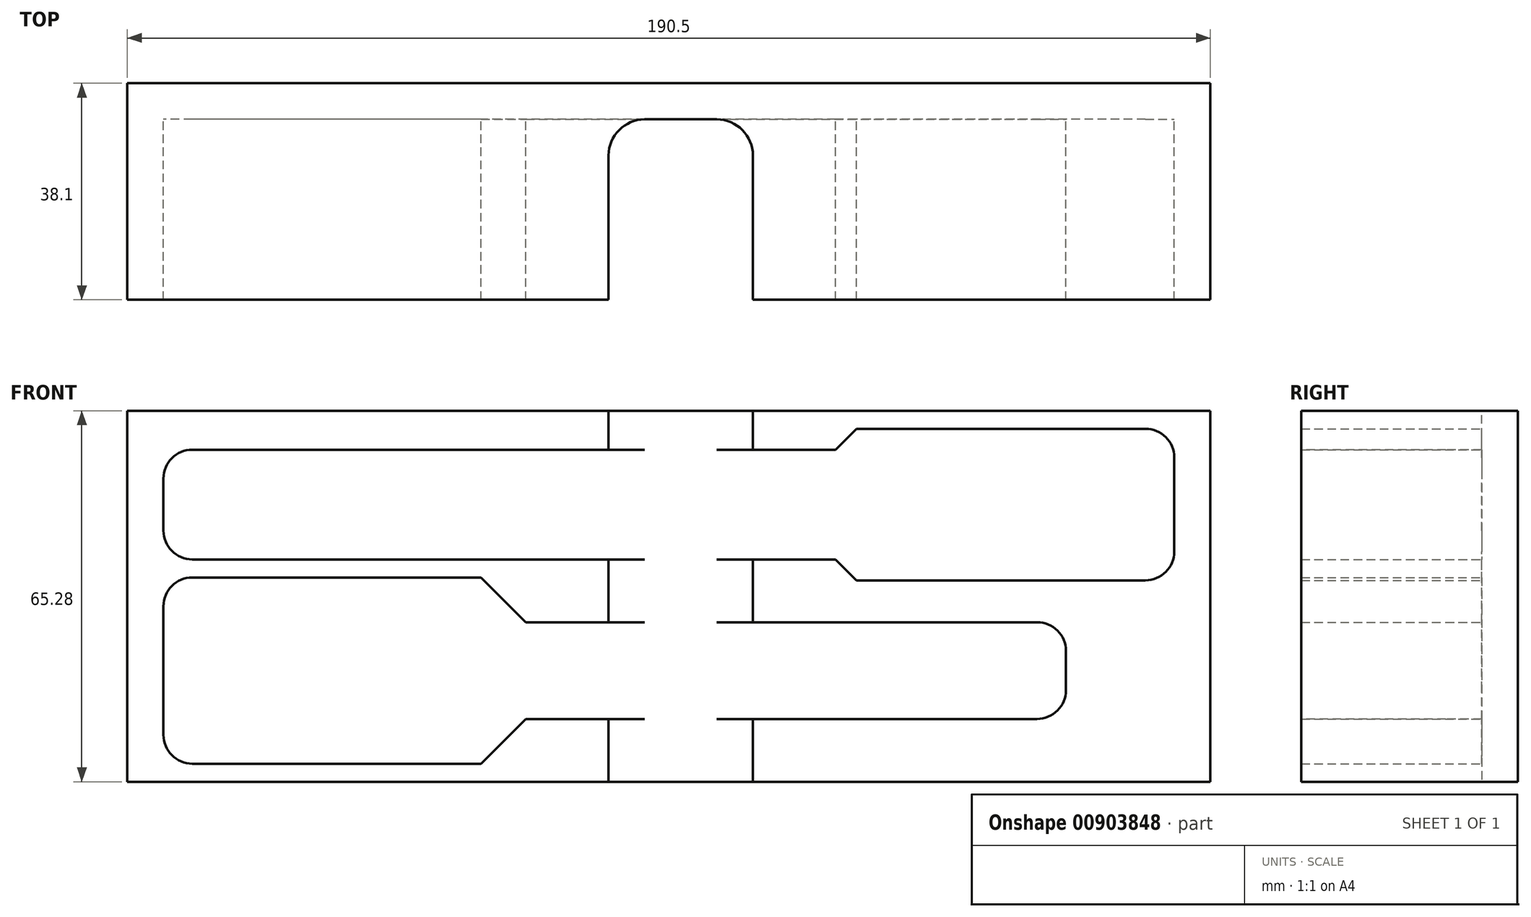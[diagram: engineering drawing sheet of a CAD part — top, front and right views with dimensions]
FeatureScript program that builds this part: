
annotation { "Feature Type Name" : "Feature", "Feature Type Description" : "" }
export const myFeature = defineFeature(function(context is Context, id is Id, definition is map)
    precondition{}
    {
        {
            var Q0;
            Q0=qCreatedBy(makeId("Front.planeOp"),FACE);
            var sketch = newSketch(context, id + "F0", { "sketchPlane" : qUnion([Q0])});
            skLineSegment(sketch, "E0.bottom", {"start": v(95.25, 32.64) * mm, "end": v(-95.25, 32.64) * mm});
            skLineSegment(sketch, "E0.top", {"start": v(95.25, -32.64) * mm, "end": v(-95.25, -32.64) * mm});
            skLineSegment(sketch, "E0.left", {"start": v(95.25, 32.64) * mm, "end": v(95.25, -32.64) * mm});
            skLineSegment(sketch, "E0.right", {"start": v(-95.25, 32.64) * mm, "end": v(-95.25, -32.64) * mm});
            skPoint(sketch, "E0.middle", {"position": v(0, 0) * mm});
            skSolve(sketch);
        }
        {
            var Q0;
            Q0 = qSketchRegion(id + "F0", true);
            extrude(context, id + "F1", {"entities" : qUnion([Q0]), "depth" : 31.75 * mm, "offsetDistance" : 25.4 * mm, "hasSecondDirection" : true, "secondDirectionOppositeDirection" : true, "secondDirectionDepth" : 6.35 * mm});
        }
        {
            var Q0;
            Q0=qCreatedBy(makeId("Front.planeOp"),FACE);
            var sketch = newSketch(context, id + "F2", { "sketchPlane" : qUnion([Q0])});
            skLineSegment(sketch, "E1", {"start": v(-88.9, 25.78) * mm, "end": v(29.34, 25.78) * mm});
            skLineSegment(sketch, "E2", {"start": v(29.34, 25.78) * mm, "end": v(33.02, 29.46) * mm});
            skLineSegment(sketch, "E3", {"start": v(33.02, 29.46) * mm, "end": v(88.9, 29.46) * mm});
            skLineSegment(sketch, "E4", {"start": v(88.9, 29.46) * mm, "end": v(88.9, 2.8) * mm});
            skLineSegment(sketch, "E5", {"start": v(88.9, 2.8) * mm, "end": v(33.02, 2.8) * mm});
            skLineSegment(sketch, "E6", {"start": v(33.02, 2.8) * mm, "end": v(29.34, 6.48) * mm});
            skLineSegment(sketch, "E7", {"start": v(29.34, 6.48) * mm, "end": v(-88.9, 6.48) * mm});
            skLineSegment(sketch, "E8", {"start": v(-88.9, 6.48) * mm, "end": v(-88.9, 25.78) * mm});
            skLineSegment(sketch, "E9", {"start": v(-88.9, 3.3) * mm, "end": v(-88.9, -29.46) * mm});
            skLineSegment(sketch, "E10", {"start": v(-88.9, -29.46) * mm, "end": v(-33.02, -29.46) * mm});
            skLineSegment(sketch, "E11", {"start": v(-33.02, -29.46) * mm, "end": v(-25.15, -21.6) * mm});
            skLineSegment(sketch, "E12", {"start": v(-25.15, -21.6) * mm, "end": v(69.85, -21.59) * mm});
            skLineSegment(sketch, "E13", {"start": v(69.85, -21.59) * mm, "end": v(69.85, -4.57) * mm});
            skLineSegment(sketch, "E14", {"start": v(69.85, -4.57) * mm, "end": v(-25.15, -4.57) * mm});
            skLineSegment(sketch, "E15", {"start": v(-25.15, -4.57) * mm, "end": v(-33.02, 3.3) * mm});
            skLineSegment(sketch, "E16", {"start": v(-33.02, 3.3) * mm, "end": v(-88.9, 3.3) * mm});
            skSolve(sketch);
        }
        {
            var Q0;
            Q0 = qSketchRegion(id + "F2", true);
            extrude(context, id + "F3", {"entities" : qUnion([Q0]), "operationType" : NewBodyOperationType.REMOVE, "endBound" : BoundingType.UP_TO_NEXT, "depth" : 25.4 * mm, "offsetDistance" : 25.4 * mm});
        }
        {
            var Q0;
            Q0=makeQuery(id+"F3.boolean.opBoolean","COPY",EDGE,{"derivedFrom":makeQuery(id+"F3.opExtrude","SWEPT_EDGE",EDGE,{"disambiguationData":[OSD([sQuery(id+"F2.wireOp",EDGE,"E9"),sQuery(id+"F2.wireOp",EDGE,"E16")])]})});
            var Q1;
            Q1=makeQuery(id+"F3.boolean.opBoolean","COPY",EDGE,{"derivedFrom":makeQuery(id+"F3.opExtrude","SWEPT_EDGE",EDGE,{"disambiguationData":[OSD([sQuery(id+"F2.wireOp",EDGE,"E9"),sQuery(id+"F2.wireOp",EDGE,"E10")])]})});
            var Q2;
            Q2=makeQuery(id+"F3.boolean.opBoolean","COPY",EDGE,{"derivedFrom":makeQuery(id+"F3.opExtrude","SWEPT_EDGE",EDGE,{"disambiguationData":[OSD([sQuery(id+"F2.wireOp",EDGE,"E13"),sQuery(id+"F2.wireOp",EDGE,"E14")])]})});
            var Q3;
            Q3=makeQuery(id+"F3.boolean.opBoolean","COPY",EDGE,{"derivedFrom":makeQuery(id+"F3.opExtrude","SWEPT_EDGE",EDGE,{"disambiguationData":[OSD([sQuery(id+"F2.wireOp",EDGE,"E12"),sQuery(id+"F2.wireOp",EDGE,"E13")])]})});
            var Q4;
            Q4=makeQuery(id+"F3.boolean.opBoolean","COPY",EDGE,{"derivedFrom":makeQuery(id+"F3.opExtrude","SWEPT_EDGE",EDGE,{"disambiguationData":[OSD([sQuery(id+"F2.wireOp",EDGE,"E4"),sQuery(id+"F2.wireOp",EDGE,"E5")])]})});
            var Q5;
            Q5=makeQuery(id+"F3.boolean.opBoolean","COPY",EDGE,{"derivedFrom":makeQuery(id+"F3.opExtrude","SWEPT_EDGE",EDGE,{"disambiguationData":[OSD([sQuery(id+"F2.wireOp",EDGE,"E3"),sQuery(id+"F2.wireOp",EDGE,"E4")])]})});
            var Q6;
            Q6=makeQuery(id+"F3.boolean.opBoolean","COPY",EDGE,{"derivedFrom":makeQuery(id+"F3.opExtrude","SWEPT_EDGE",EDGE,{"disambiguationData":[OSD([sQuery(id+"F2.wireOp",EDGE,"E1"),sQuery(id+"F2.wireOp",EDGE,"E8")])]})});
            var Q7;
            Q7=makeQuery(id+"F3.boolean.opBoolean","COPY",EDGE,{"derivedFrom":makeQuery(id+"F3.opExtrude","SWEPT_EDGE",EDGE,{"disambiguationData":[OSD([sQuery(id+"F2.wireOp",EDGE,"E7"),sQuery(id+"F2.wireOp",EDGE,"E8")])]})});
            fillet(context, id + "F4", {"entities" : qUnion([Q0, Q1, Q2, Q3, Q4, Q5, Q6, Q7]), "radius" : 5.08 * mm, "tangentPropagation" : true, "allowEdgeOverflow" : false});
        }
        {
            var Q0;
            Q0=makeQuery(id+"F1.opExtrude","CAP_FACE",FACE,{"disambiguationData":[OSD([sQuery(id+"F0.wireOp",EDGE,"E0.bottom"),sQuery(id+"F0.wireOp",EDGE,"E0.top"),sQuery(id+"F0.wireOp",EDGE,"E0.left"),sQuery(id+"F0.wireOp",EDGE,"E0.right")])],"isStart":false});
            var sketch = newSketch(context, id + "F5", { "sketchPlane" : qUnion([Q0])});
            skLineSegment(sketch, "E17", {"start": v(-10.6, 32.64) * mm, "end": v(-10.6, -32.64) * mm});
            skLineSegment(sketch, "E18", {"start": v(-10.6, -32.64) * mm, "end": v(14.8, -32.64) * mm});
            skLineSegment(sketch, "E19", {"start": v(14.8, -32.64) * mm, "end": v(14.8, 32.64) * mm});
            skLineSegment(sketch, "E20", {"start": v(14.8, 32.64) * mm, "end": v(-10.6, 32.64) * mm});
            skLineSegment(sketch, "E21", {"start": v(-25.15, -4.57) * mm, "end": v(-10.6, -4.57) * mm, "construction": true});
            skLineSegment(sketch, "E22", {"start": v(29.34, 6.48) * mm, "end": v(14.8, 6.48) * mm, "construction": true});
            skSolve(sketch);
        }
        {
            var Q0;
            Q0 = qSketchRegion(id + "F5", true);
            extrude(context, id + "F6", {"entities" : qUnion([Q0]), "operationType" : NewBodyOperationType.REMOVE, "oppositeDirection" : true, "depth" : 31.75 * mm, "offsetDistance" : 25.4 * mm});
        }
        {
            var Q0;
            {var subQ1=sQuery(id+"F5.wireOp",EDGE,"E19");Q0=makeQuery(id+"F6.boolean.opBoolean","COPY",EDGE,{"disambiguationData":[TD([makeQuery(id+"F1.opExtrude","SWEPT_FACE",FACE,{"disambiguationData":[OSD([sQuery(id+"F0.wireOp",EDGE,"E0.top")])]})])],"derivedFrom":makeQuery(id+"F6.opExtrude","CAP_EDGE",EDGE,{"disambiguationData":[OSD([subQ1])],"isStart":false})});}
            var Q1;
            {var subQ1=sQuery(id+"F2.wireOp",EDGE,"E7");var subQ2=sQuery(id+"F5.wireOp",EDGE,"E19");Q1=makeQuery(id+"F6.boolean.opBoolean","COPY",EDGE,{"disambiguationData":[TD([makeQuery(id+"F3.boolean.opBoolean","COPY",FACE,{"derivedFrom":makeQuery(id+"F3.opExtrude","SWEPT_FACE",FACE,{"disambiguationData":[OSD([subQ1])]})})])],"derivedFrom":makeQuery(id+"F6.opExtrude","CAP_EDGE",EDGE,{"disambiguationData":[OSD([subQ2])],"isStart":false})});}
            var Q2;
            {var subQ1=sQuery(id+"F5.wireOp",EDGE,"E19");Q2=makeQuery(id+"F6.boolean.opBoolean","COPY",EDGE,{"disambiguationData":[TD([makeQuery(id+"F1.opExtrude","SWEPT_FACE",FACE,{"disambiguationData":[OSD([sQuery(id+"F0.wireOp",EDGE,"E0.bottom")])]})])],"derivedFrom":makeQuery(id+"F6.opExtrude","CAP_EDGE",EDGE,{"disambiguationData":[OSD([subQ1])],"isStart":false})});}
            var Q3;
            {var subQ1=sQuery(id+"F5.wireOp",EDGE,"E17");Q3=makeQuery(id+"F6.boolean.opBoolean","COPY",EDGE,{"disambiguationData":[TD([makeQuery(id+"F1.opExtrude","SWEPT_FACE",FACE,{"disambiguationData":[OSD([sQuery(id+"F0.wireOp",EDGE,"E0.bottom")])]})])],"derivedFrom":makeQuery(id+"F6.opExtrude","CAP_EDGE",EDGE,{"disambiguationData":[OSD([subQ1])],"isStart":false})});}
            var Q4;
            {var subQ1=sQuery(id+"F2.wireOp",EDGE,"E7");var subQ2=sQuery(id+"F5.wireOp",EDGE,"E17");Q4=makeQuery(id+"F6.boolean.opBoolean","COPY",EDGE,{"disambiguationData":[TD([makeQuery(id+"F3.boolean.opBoolean","COPY",FACE,{"derivedFrom":makeQuery(id+"F3.opExtrude","SWEPT_FACE",FACE,{"disambiguationData":[OSD([subQ1])]})})])],"derivedFrom":makeQuery(id+"F6.opExtrude","CAP_EDGE",EDGE,{"disambiguationData":[OSD([subQ2])],"isStart":false})});}
            var Q5;
            {var subQ1=sQuery(id+"F5.wireOp",EDGE,"E17");Q5=makeQuery(id+"F6.boolean.opBoolean","COPY",EDGE,{"disambiguationData":[TD([makeQuery(id+"F1.opExtrude","SWEPT_FACE",FACE,{"disambiguationData":[OSD([sQuery(id+"F0.wireOp",EDGE,"E0.top")])]})])],"derivedFrom":makeQuery(id+"F6.opExtrude","CAP_EDGE",EDGE,{"disambiguationData":[OSD([subQ1])],"isStart":false})});}
            fillet(context, id + "F7", {"entities" : qUnion([Q0, Q1, Q2, Q3, Q4, Q5]), "radius" : 6.35 * mm, "tangentPropagation" : true, "allowEdgeOverflow" : false});
        }
    });
